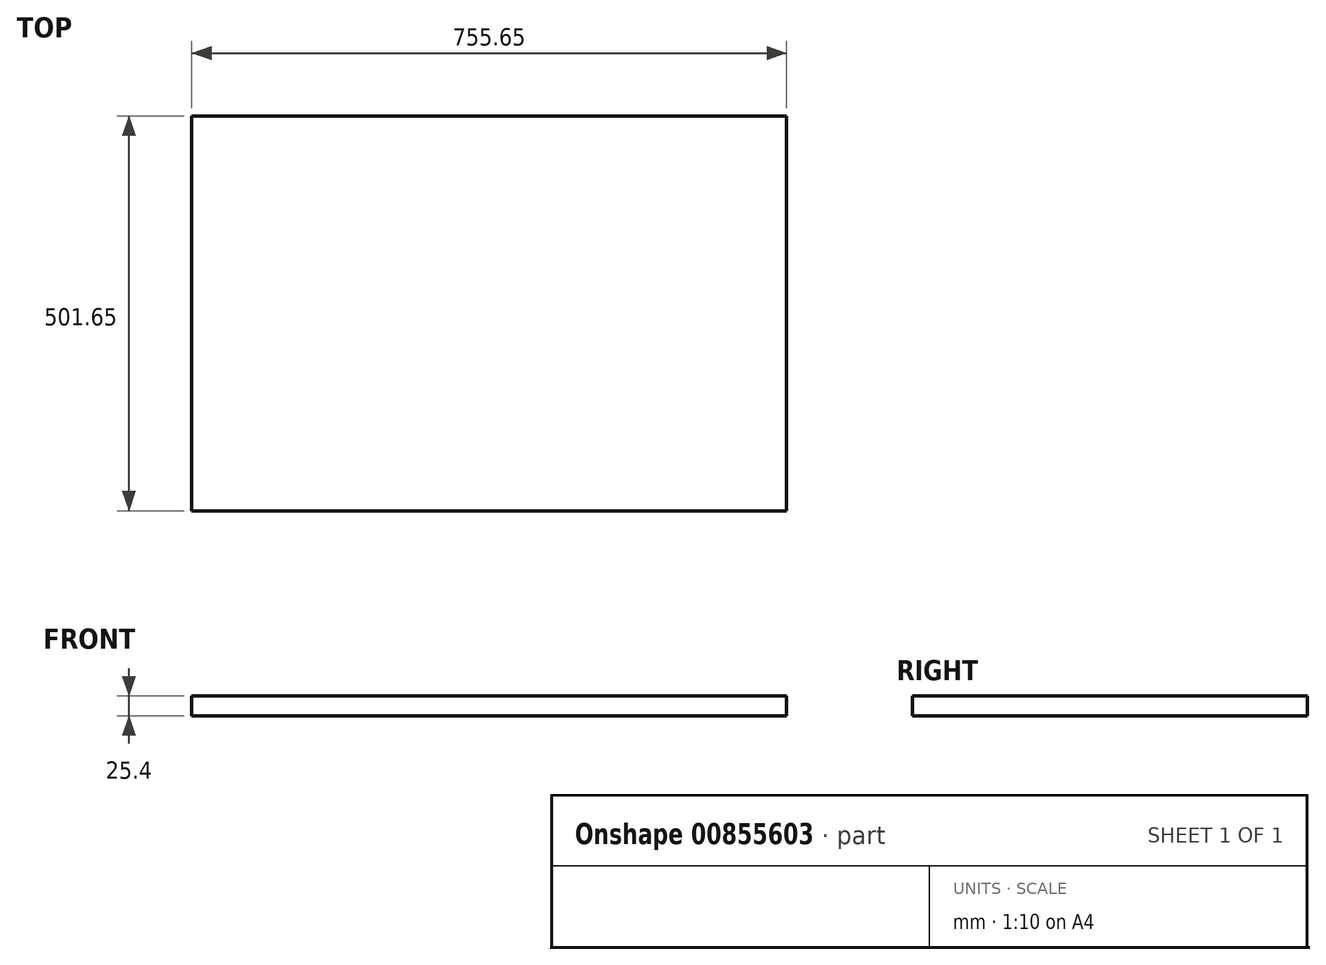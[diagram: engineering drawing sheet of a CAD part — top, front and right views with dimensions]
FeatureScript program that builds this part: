
annotation { "Feature Type Name" : "Feature", "Feature Type Description" : "" }
export const myFeature = defineFeature(function(context is Context, id is Id, definition is map)
    precondition{}
    {
        {
            var Q0;
            Q0=qCreatedBy(makeId("Top.planeOp"),FACE);
            var sketch = newSketch(context, id + "F0", { "sketchPlane" : qUnion([Q0])});
            skLineSegment(sketch, "E0.bottom", {"start": v(0, 0) * mm, "end": v(755.65, 0) * mm});
            skLineSegment(sketch, "E0.top", {"start": v(0, 501.65) * mm, "end": v(755.65, 501.65) * mm});
            skLineSegment(sketch, "E0.left", {"start": v(0, 0) * mm, "end": v(0, 501.65) * mm});
            skLineSegment(sketch, "E0.right", {"start": v(755.65, 0) * mm, "end": v(755.65, 501.65) * mm});
            skSolve(sketch);
        }
        {
            var Q0;
            Q0=qSketchRegion(id+"F0",true);
            extrude(context, id + "F1", {"entities" : qUnion([Q0]), "depth" : 25.4 * mm, "offsetDistance" : 25.4 * mm});
        }
    });
